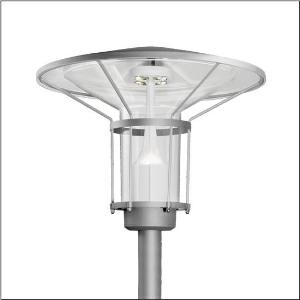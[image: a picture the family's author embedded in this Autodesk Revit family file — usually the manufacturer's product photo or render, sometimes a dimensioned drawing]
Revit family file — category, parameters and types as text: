
# Revit family: laterne_classic_iq___p1_0a_5xa5245ff14h000022_892e
name_source: partatom
category: Lighting Fixtures
units: mm (PartAtom-declared; Revit-internal decimal feet)

## family parameters
Cut with Voids When Loaded = No
Host = Face
Light Source = No
Part Type = Normal
Room Calculation Point = No
Round Connector Dimension = Use Diameter
Shared = No

## types (1)
- --- (1 x LED, 1360 lm, 10.5 W, 3000K)
    Apparent Load = 11 VA
    CIE Flux Codes = 30 61 91 96 100
    Color Rendering = 70
    Color Temperature = 3000K
    Default Elevation = 1800 mm
    Description = Lantern Classic iQ, mast luminaire, Module 540 iQ-SR, primary light control with 3 zone facetted reflector, of plastic, silver coated, highly specular, structured, primary optical cover: cover, of PMMA, transparent, light distribution: P1.0a, light emission: direct distribution, primary light characteristic: strongly asymmetric, installation type: post-top, LED, High Power LED, rated luminous flux: 1.360lm, luminous efficacy: 130lm/W, light colour: 730, colour temperature: 3000K, control gear: iQ Street-Remote, control: Street-Remote, Auto-Match, Temp-Guard, Lumen-Switch, Night-Set, Smart-Wire, Light-Fading, Desk-Remote (wireless, voltage-free reading and setting of iQ features in the workshop via application-optimized NFC function/RFID function), optimised constant luminous flux control (CLO 2.0), pre-setting: logarithmic dimming characteristic, mains connection: 230..240V, AC, 50/60Hz, connection cable pre-assembled, cable length: 5,5m, wiring characteristics: H07RN-F, start of lifetime: 11W, end of service life: 11W, reduction: 5W, luminaire housing, upper part, of glass-fibre reinforced polyester, coated, Siteco® metallic grey (DB 702S), diameter: 750mm, height: 596mm, spigot size: d x l = 76 x 70mm (post-top) | with reducer (optional accessory) 60 x 70mm, mounting height: 3..5m, post-top mast mounting element, of diecast aluminium, coated, Siteco® metallic grey (DB 702S), Module 540 iQ-SR, traffic white (RAL 9016), equipment: standard, protection rating (complete): IP65, insulation class (complete): insulation class II (safety insulation), certification: CE, ENEC, VDE, packaging unit: 1 piece

Light Distribution: P1.0a
    Height = 596 mm
    Lamp = 1 x LED
    Lamp Light Flux = 1360 lm
    Lamp Power = 10.5 W
    Lamp count = 1
    Length = 750 mm
    Luminous efficacy = 130 lm/W
    Manufacturer = Siteco
    ModVariant = No
    Model = 5XA5245FF14H000022
    Number of Poles = 1
    OnlyDefault = Yes
    Power Factor = 1
    Product Name = Laterne Classic iQ | P1.0a
    Product group = mast luminaire | pylon top
    ProductGroupID = 6100
    Protection Class = Protection class II
    Protection Degree = IP 65
    RLX_Detail_Level = 1
    RLX_Emergency_Light_Flux = 0 lm
    RLX_Emergency_Type = 0
    RLX_Emergency_Type_DB = No
    RlxData = <blob elided: 64585 chars, md5=c86baa74>
    Socket = socket
    Standby Power = 0 W
    System Light Flux = 1360 lm
    System Power = 11 W
    Type Comments = factory setting: luminous flux: 100 % | dim-lin: 254 | 419 mA
    Type Image = l_1006052.jpg
    URL = http://relux.com
    VarID = @adj_155836
    Voltage = 0 V
    Weight = 0.00 kg
    Width = 0 mm  [stored 0 ft]

note: [stored X ft] marks values corroborated as IEEE doubles in the binary element streams (Revit-internal decimal feet)

## geometry (parser evidence)
native form markers: Blend x4, Sweep x10
no freeform markers — native parametric forms only
